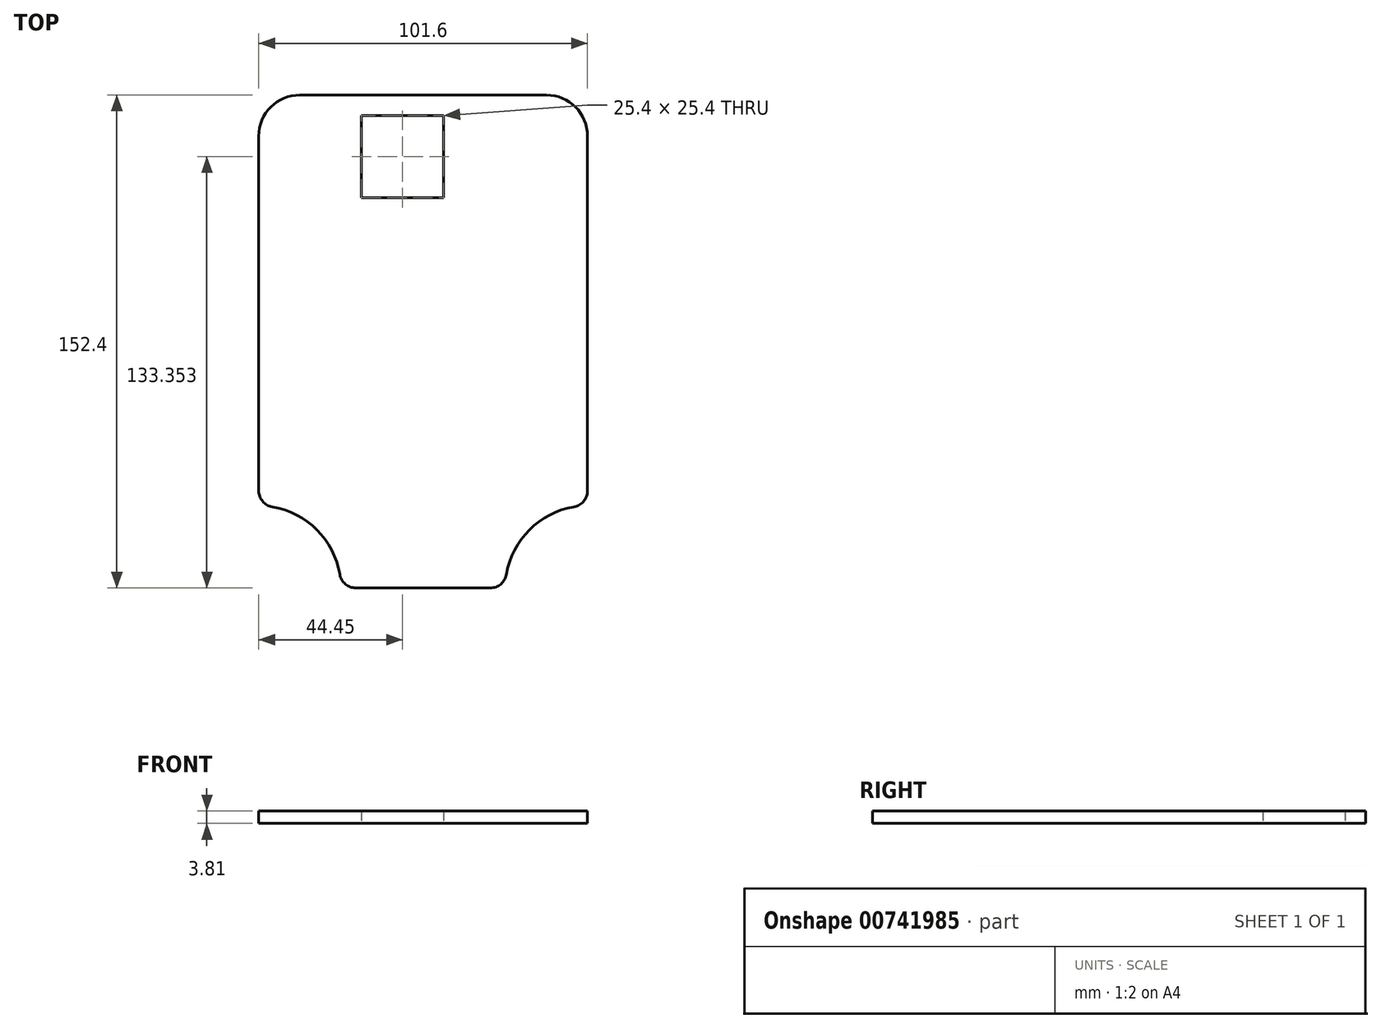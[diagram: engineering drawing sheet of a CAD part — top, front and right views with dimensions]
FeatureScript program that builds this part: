
annotation { "Feature Type Name" : "Feature", "Feature Type Description" : "" }
export const myFeature = defineFeature(function(context is Context, id is Id, definition is map)
    precondition{}
    {
        {
            var Q0;
            Q0=qCreatedBy(makeId("Top.planeOp"),FACE);
            var sketch = newSketch(context, id + "F0", { "sketchPlane" : qUnion([Q0])});
            skLineSegment(sketch, "E0.bottom", {"start": v(-57.15, 96.3) * mm, "end": v(44.45, 96.3) * mm});
            skLineSegment(sketch, "E0.top", {"start": v(-57.15, -56.1) * mm, "end": v(44.45, -56.1) * mm});
            skLineSegment(sketch, "E0.left", {"start": v(-57.15, 96.3) * mm, "end": v(-57.15, -56.1) * mm});
            skLineSegment(sketch, "E0.right", {"start": v(44.45, 96.3) * mm, "end": v(44.45, -56.1) * mm});
            skCircle(sketch, "E1", {"center": v(-57.15, -56.1) * mm, "radius": 25.4 * mm});
            skCircle(sketch, "E2", {"center": v(44.45, -56.1) * mm, "radius": 25.4 * mm});
            skLineSegment(sketch, "E3", {"start": v(-57.15, 96.3) * mm, "end": v(-57.15, 70.9) * mm});
            skLineSegment(sketch, "E4", {"start": v(-57.15, 96.3) * mm, "end": v(-12.7, 96.3) * mm});
            skLineSegment(sketch, "E5", {"start": v(-12.7, 96.3) * mm, "end": v(0, 96.3) * mm});
            skLineSegment(sketch, "E6", {"start": v(0, 96.3) * mm, "end": v(44.45, 96.3) * mm});
            skLineSegment(sketch, "E7", {"start": v(-57.15, 83.6) * mm, "end": v(-57.15, 89.95) * mm});
            skLineSegment(sketch, "E8", {"start": v(-57.15, 89.95) * mm, "end": v(-25.4, 89.95) * mm});
            skLineSegment(sketch, "E9.bottom", {"start": v(-25.4, 89.95) * mm, "end": v(0, 89.95) * mm});
            skLineSegment(sketch, "E9.top", {"start": v(-25.4, 64.55) * mm, "end": v(0, 64.55) * mm});
            skLineSegment(sketch, "E9.left", {"start": v(-25.4, 89.95) * mm, "end": v(-25.4, 64.55) * mm});
            skLineSegment(sketch, "E9.right", {"start": v(0, 89.95) * mm, "end": v(0, 64.55) * mm});
            skSolve(sketch);
        }
        {
            var Q0;
            {var subQ1=sQuery(id+"F0.wireOp",EDGE,"E0.bottom");Q0=makeQuery(id+"F0.imprint","IMPRINT",FACE,{"disambiguationData":[TD([[makeQuery(id+"F0.imprint","IMPRINT",EDGE,{"derivedFrom":subQ1}),-1.0]])]});}
            var Q1;
            {var subQ1=sQuery(id+"F0.wireOp",EDGE,"E4");Q1=makeQuery(id+"F0.imprint","IMPRINT",FACE,{"disambiguationData":[TD([[makeQuery(id+"F0.imprint","IMPRINT",EDGE,{"derivedFrom":subQ1}),-1.0]])]});}
            extrude(context, id + "F1", {"entities" : qUnion([Q0, Q1]), "depth" : 3.8 * mm, "offsetDistance" : 25.4 * mm});
        }
        {
            var Q0;
            Q0=makeQuery(id+"F1.opExtrude","SWEPT_EDGE",EDGE,{"disambiguationData":[OSD([sQuery(id+"F0.wireOp",EDGE,"E0.left"),sQuery(id+"F0.wireOp",EDGE,"E1")])]});
            var Q1;
            Q1=makeQuery(id+"F1.opExtrude","SWEPT_EDGE",EDGE,{"disambiguationData":[OSD([sQuery(id+"F0.wireOp",EDGE,"E0.top"),sQuery(id+"F0.wireOp",EDGE,"E1")])]});
            fillet(context, id + "F2", {"entities" : qUnion([Q0, Q1]), "radius" : 5.08 * mm, "tangentPropagation" : true, "allowEdgeOverflow" : false});
        }
        {
            var Q0;
            Q0=makeQuery(id+"F1.opExtrude","SWEPT_EDGE",EDGE,{"disambiguationData":[OSD([sQuery(id+"F0.wireOp",EDGE,"E0.right"),sQuery(id+"F0.wireOp",EDGE,"E2")])]});
            var Q1;
            Q1=makeQuery(id+"F1.opExtrude","SWEPT_EDGE",EDGE,{"disambiguationData":[OSD([sQuery(id+"F0.wireOp",EDGE,"E0.top"),sQuery(id+"F0.wireOp",EDGE,"E2")])]});
            fillet(context, id + "F3", {"entities" : qUnion([Q0, Q1]), "radius" : 5.08 * mm, "tangentPropagation" : true, "allowEdgeOverflow" : false});
        }
        {
            var Q0;
            Q0=makeQuery(id+"F1.opExtrude","SWEPT_EDGE",EDGE,{"disambiguationData":[OSD([sQuery(id+"F0.wireOp",EDGE,"E0.bottom"),sQuery(id+"F0.wireOp",EDGE,"E0.left")])]});
            var Q1;
            Q1=makeQuery(id+"F1.opExtrude","SWEPT_EDGE",EDGE,{"disambiguationData":[OSD([sQuery(id+"F0.wireOp",EDGE,"E0.bottom"),sQuery(id+"F0.wireOp",EDGE,"E0.right")])]});
            var Q2;
            Q2=makeQuery(id+"F1.opExtrude","SWEPT_EDGE",EDGE,{"disambiguationData":[OSD([sQuery(id+"F0.wireOp",EDGE,"E3"),sQuery(id+"F0.wireOp",EDGE,"E4")])]});
            fillet(context, id + "F4", {"entities" : qUnion([Q0, Q1, Q2]), "radius" : 12.7 * mm, "tangentPropagation" : true, "allowEdgeOverflow" : false});
        }
    });
